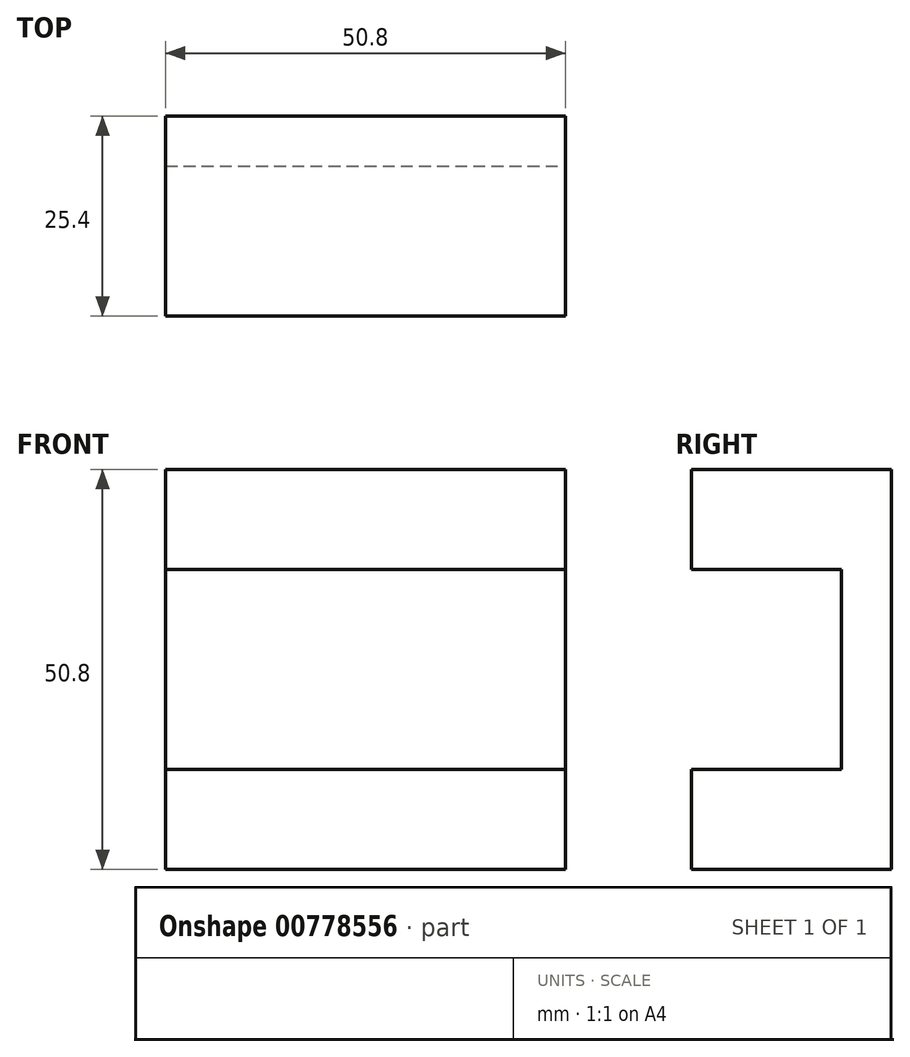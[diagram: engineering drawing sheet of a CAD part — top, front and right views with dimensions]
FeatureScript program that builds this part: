
annotation { "Feature Type Name" : "Feature", "Feature Type Description" : "" }
export const myFeature = defineFeature(function(context is Context, id is Id, definition is map)
    precondition{}
    {
        {
            var Q0;
            Q0=qCreatedBy(makeId("Top.planeOp"),FACE);
            var sketch = newSketch(context, id + "F0", { "sketchPlane" : qUnion([Q0])});
            skLineSegment(sketch, "E0.bottom", {"start": v(25.4, 12.7) * mm, "end": v(-25.4, 12.7) * mm});
            skLineSegment(sketch, "E0.top", {"start": v(25.4, -12.7) * mm, "end": v(-25.4, -12.7) * mm});
            skLineSegment(sketch, "E0.left", {"start": v(25.4, 12.7) * mm, "end": v(25.4, -12.7) * mm});
            skLineSegment(sketch, "E0.right", {"start": v(-25.4, 12.7) * mm, "end": v(-25.4, -12.7) * mm});
            skPoint(sketch, "E0.middle", {"position": v(0, 0) * mm});
            skSolve(sketch);
        }
        {
            var Q0;
            Q0=makeQuery(id+"F0.imprint","IMPRINT",FACE,{"disambiguationData":[TD([[makeQuery(id+"F0.imprint","IMPRINT",EDGE,{"derivedFrom":sQuery(id+"F0.wireOp",EDGE,"E0.bottom")}),1.0]])]});
            extrude(context, id + "F1", {"entities" : qUnion([Q0]), "depth" : 50.8 * mm, "offsetDistance" : 25.4 * mm});
        }
        {
            var Q0;
            Q0=makeQuery(id+"F1.opExtrude","SWEPT_FACE",FACE,{"disambiguationData":[OSD([sQuery(id+"F0.wireOp",EDGE,"E0.left")])]});
            var sketch = newSketch(context, id + "F2", { "sketchPlane" : qUnion([Q0])});
            skLineSegment(sketch, "E1", {"start": v(-12.7, 12.7) * mm, "end": v(6.35, 12.7) * mm});
            skLineSegment(sketch, "E2", {"start": v(6.35, 12.7) * mm, "end": v(6.35, 38.1) * mm});
            skLineSegment(sketch, "E3", {"start": v(6.35, 38.1) * mm, "end": v(-12.7, 38.1) * mm});
            skLineSegment(sketch, "E4", {"start": v(-12.7, 38.1) * mm, "end": v(-12.7, 12.7) * mm});
            skSolve(sketch);
        }
        {
            var Q0;
            Q0=makeQuery(id+"F2.imprint","IMPRINT",FACE,{"disambiguationData":[TD([[makeQuery(id+"F2.imprint","IMPRINT",EDGE,{"derivedFrom":sQuery(id+"F2.wireOp",EDGE,"E1")}),1.0]])]});
            var Q1;
            Q1=makeQuery(id+"F1.opExtrude","SWEPT_FACE",FACE,{"disambiguationData":[OSD([sQuery(id+"F0.wireOp",EDGE,"E0.right")])]});
            extrude(context, id + "F3", {"entities" : qUnion([Q0]), "operationType" : NewBodyOperationType.REMOVE, "endBound" : BoundingType.UP_TO_SURFACE, "oppositeDirection" : true, "depth" : 25.4 * mm, "endBoundEntityFace" : qUnion([Q1]), "offsetDistance" : 25.4 * mm});
        }
    });
